# Revit family: Haworth_Pergola_Drapery_Radial
name_source: partatom
category: Furniture Systems
revit_build: Autodesk Revit 2018 (Build: 20170223_1515(x64)
units: mm (PartAtom-declared; Revit-internal decimal feet)

## family parameters
Always vertical = Yes
Cut with Voids When Loaded = No
OmniClass Number = 23.40.70.14.64.21
OmniClass Title = Systems Furniture
Part Type = Normal
Room Calculation Point = No
Round Connector Dimension = Use Diameter
Shared = No
Work Plane-Based = No

## types (2) — shared parameters
Actual Depth = 4"
Actual Height = 91 1/4"
Actual Width = 72"
Array Count = 19
Assembly Code = E2020200
Base Height = 1 1/2"
Bracket Thickness = 25/128"
Curtain Finish = Haworth _ Fabic _ Undecided _ Pergola
Description = Haworth - Pergola Drapery - Radial
Drapery Top Offset = 1/2"
End RP Angle = 2.33°
End Slat Offset = 3"
Manufacturer = Haworth
Max. Height = 89 1/2"
Max. Width = 72"
Min. Height = 89 1/2"
Min. Width = 72"
Model = Haworth Pergola
Revision Number = 1
Size = Verify Final Dim. w/ Haworth
Slat Center Offset = 71 251/256"
Slat Count = 12
Standard Radius = 72 in.
Sustainability Info = http://www.haworth.com
Trim Finish = Haworth _ Paint _ Undecided _ Pergola
URL = http://www.haworth.com
URL - Product = https://www.haworth.com
Warranty = http://www.haworth.com

## per-type parameters (varying)
| type | Closed Drapery | Half Open Drapery |
| 72 in. radius - Half Open Drapery | No | Yes |
| 72 in. radius - Closed Drapery | Yes | No |

## geometry (parser evidence)
native form markers: Sweep x4
no freeform markers — native parametric forms only
